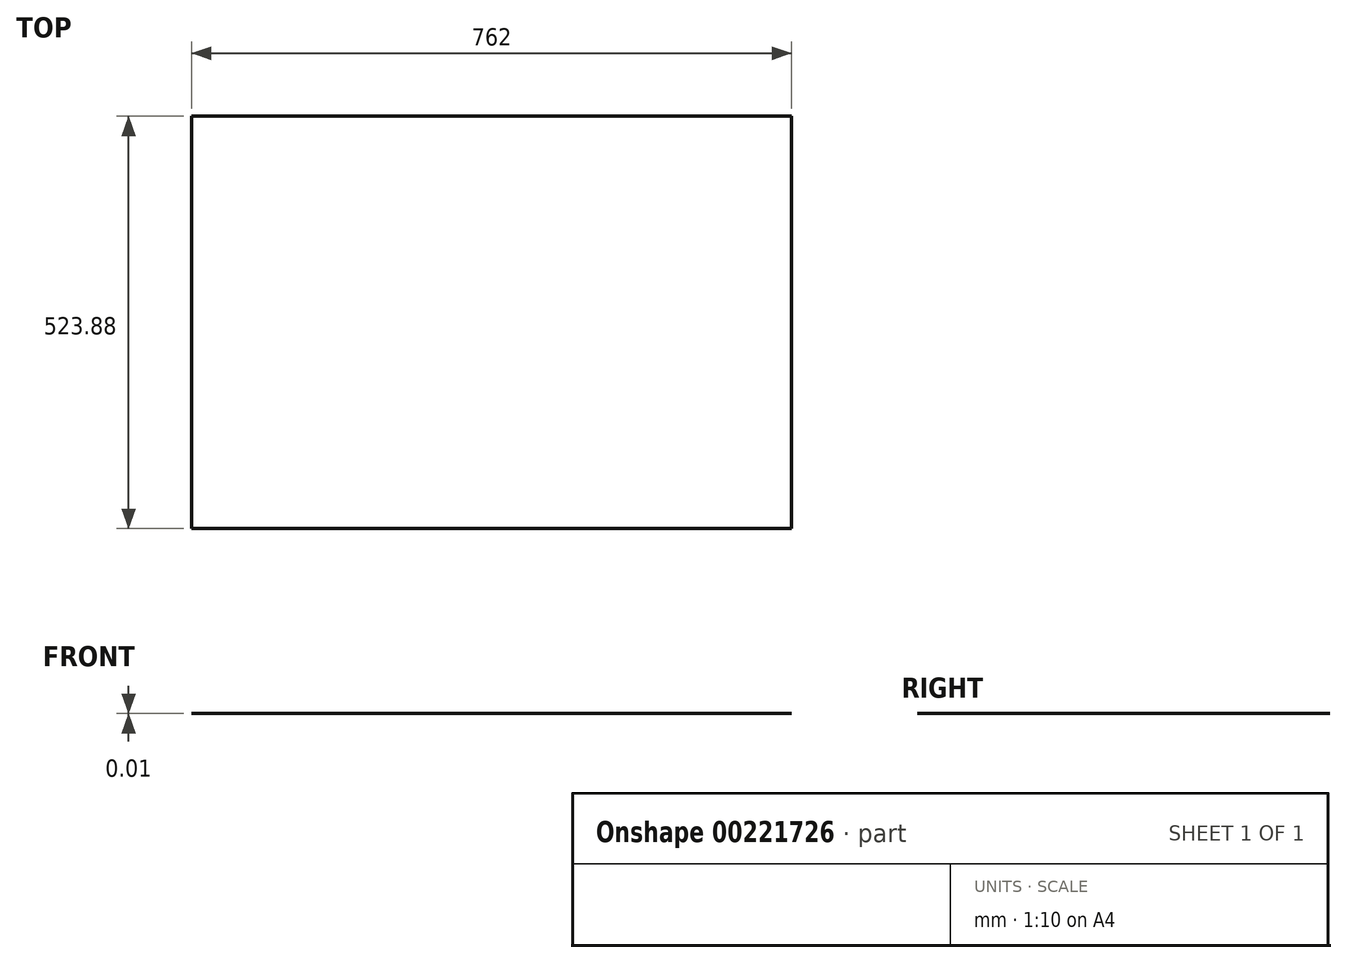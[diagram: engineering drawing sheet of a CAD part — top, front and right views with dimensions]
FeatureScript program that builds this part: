
annotation { "Feature Type Name" : "Feature", "Feature Type Description" : "" }
export const myFeature = defineFeature(function(context is Context, id is Id, definition is map)
    precondition{}
    {
        {
            var Q0;
            Q0=qCreatedBy(makeId("Top.planeOp"),FACE);
            var sketch = newSketch(context, id + "F0", { "sketchPlane" : qUnion([Q0])});
            skLineSegment(sketch, "E0.bottom", {"start": v(-914.71, -256.16) * mm, "end": v(-152.71, -256.16) * mm});
            skLineSegment(sketch, "E0.top", {"start": v(-914.71, 267.72) * mm, "end": v(-152.71, 267.72) * mm});
            skLineSegment(sketch, "E0.left", {"start": v(-914.71, -256.16) * mm, "end": v(-914.71, 267.72) * mm});
            skLineSegment(sketch, "E0.right", {"start": v(-152.71, -256.16) * mm, "end": v(-152.71, 267.72) * mm});
            skSolve(sketch);
        }
        {
            var Q0;
            Q0 = qSketchRegion(id + "F0", true);
            extrude(context, id + "F1", {"entities" : qUnion([Q0]), "oppositeDirection" : true, "depth" : 3 / 406.4 * mm});
        }
    });
